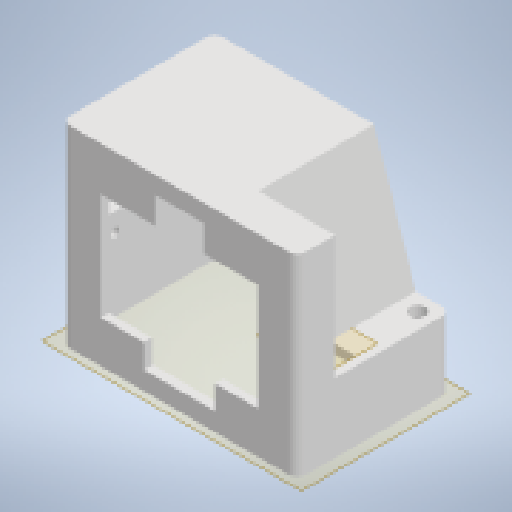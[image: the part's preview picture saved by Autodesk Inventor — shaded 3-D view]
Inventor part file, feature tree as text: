
AUTODESK INVENTOR PART (.ipt)
format: ipt  version: 2024 (Build 280153000, 153)  size: 499,200 bytes
history: native  units: mm
features: sketch x21, extrude x20, projected_geometry x18, reference x11, other x6, plane x2, fillet x1
ambient origin geometry x8: Origin, YZ Plane, XZ Plane, XY Plane, X Axis, Y Axis, Z Axis, Center Point
bodies: Volumenkörper1 (feature_tree)
feature tree (79):
  plane  "Arbeitsebene1"
  extrude  "Extrusion1"  Depth=2.2mm TaperAngle=0.0deg
  extrude  "Extrusion2"  Depth=38.0mm
  extrude  "Extrusion3"  Depth=2.0mm
  extrude  "Extrusion4"  Depth=7.82mm
  extrude  "Extrusion5"  Depth=0.2mm
  extrude  "Extrusion6"  Depth=0.2mm
  extrude  "Extrusion7"  Depth=0.3mm
  extrude  "Extrusion8"  Depth=1.8mm
  extrude  "Extrusion9"  Depth=10.0mm TaperAngle=0.0deg
  extrude  "Extrusion10"  Depth=8.0mm
  extrude  "Extrusion11"  Depth=8.0mm
  fillet  "Rundung1"  Radius=5.5mm
  plane  "Arbeitsebene2"
  extrude  "Extrusion12"  Depth=2.0mm
  extrude  "Extrusion13"  Depth=10.0mm TaperAngle=0.0deg
  extrude  "Extrusion14"  Depth=2.0mm
  extrude  "Extrusion15"  Depth=10.0mm TaperAngle=0.0deg
  extrude  "Extrusion16"  Depth=2.0mm TaperAngle=0.0deg
  extrude  "Extrusion17"  Depth=2.0mm TaperAngle=0.0deg
  extrude  "Extrusion18"  Depth=2.0mm TaperAngle=0.0deg
  sketch  "Skizze21"  dims[d57=2.0mm d58=2.0mm d59=0.0mm]
  extrude  "Extrusion19"  Depth=2.0mm TaperAngle=0.0deg
  extrude  "Extrusion20"  Depth=10.0mm TaperAngle=0.0deg
  sketch  "Skizze1"  dims[d0=0.2mm d1=2.2mm d2=0.0mm]
  reference  "Referenz1"
  sketch  "Skizze2"  dims[d3=38.0mm d4=0.0mm d5=36.0mm]
  reference  "Referenz2"
  reference  "Referenz3"
  projected_geometry  "Projizierte Kontur1"
  sketch  "Skizze3"  dims[d6=34.0mm d7=2.0mm]
  reference  "Referenz4"
  sketch  "Skizze4"  dims[d8=7.82mm d9=7.82mm]
  projected_geometry  "Projizierte Kontur2"
  sketch  "Skizze5"  dims[d10=38.0mm d11=0.0mm d12=0.2mm]
  projected_geometry  "Projizierte Kontur3"
  reference  "Referenz5"
  sketch  "Skizze6"  dims[d13=10.0mm d14=0.0mm d15=0.2mm]
  reference  "Referenz6"
  sketch  "Skizze7"  dims[d16=0.5mm d17=0.3mm]
  projected_geometry  "Projizierte Kontur4"
  sketch  "Skizze8"  dims[d18=1.8mm d19=0.0mm d20=1.6mm]
  reference  "Referenz7"
  reference  "Referenz8"
  sketch  "Skizze9"  dims[d21=1.8mm d22=0.0mm d23=10.0mm d24=0.0mm]
  projected_geometry  "Projizierte Kontur5"
  projected_geometry  "Projizierte Kontur6"
  sketch  "Skizze10"  dims[d25=2.5mm d26=8.0mm]
  sketch  "Skizze11"  dims[d27=2.5mm d28=8.0mm d29=5.5mm d30=0.0mm]
  projected_geometry  "Projizierte Kontur7"
  projected_geometry  "Projizierte Kontur8"
  sketch  "Skizze12"  dims[d31=3.5mm d32=2.0mm]
  reference  "Referenz9"
  sketch  "Skizze13"  dims[d33=5.5mm d34=0.0mm d35=10.0mm d36=0.0mm]
  projected_geometry  "Projizierte Kontur9"
  projected_geometry  "Projizierte Kontur10"
  projected_geometry  "Projizierte Kontur11"
  projected_geometry  "Projizierte Kontur12"
  reference  "Referenz10"
  sketch  "Skizze15"  dims[d37=1.0mm d38=0.0mm d39=2.0mm]
  projected_geometry  "Projizierte Kontur14"
  sketch  "Skizze17"  dims[d40=1.0mm d41=0.0mm d42=10.0mm d43=0.0mm]
  projected_geometry  "Projizierte Kontur16"
  sketch  "Skizze18"  dims[d46=2.0mm d47=0.0mm d49=2.0mm d50=0.0mm]
  projected_geometry  "Projizierte Kontur17"
  sketch  "Skizze19"  dims[d51=2.0mm d52=2.0mm d53=0.0mm]
  projected_geometry  "Projizierte Kontur18"
  sketch  "Skizze20"  dims[d54=6.5mm d55=2.0mm d56=0.0mm]
  sketch  "Skizze22"  dims[d60=1.0mm d61=0.0mm d62=10.0mm d63=0.0mm]
  projected_geometry  "Projizierte Kontur19"
  projected_geometry  "Projizierte Kontur20"
  sketch  "Skizze23"
  reference  "Referenz11"
  parser-record x1  (decoder bookkeeping rows leaked as tree rows — omitted from the tree; the rows remain in map.json)
  other  "main.iam"
  other  "Gehaeuse_unten:1"
  other  "Oled SH1106:1"
  other  "ESP32-C3 supermini v5:2"
  other  "GY-BME280:1"
note: 1 file-system path scrubbed to <path> (originals preserved in map.json)
